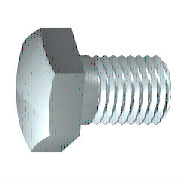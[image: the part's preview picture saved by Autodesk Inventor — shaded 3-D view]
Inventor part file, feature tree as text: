
AUTODESK INVENTOR PART (.ipt)
format: ipt  version: 2025.1 (Build 291241020, 241B)  size: 198,144 bytes
history: native  units: mm (DEFAULTED — no unit token found)
features: extrude x1, chamfer x1, plane x1
ambient origin geometry x7: Origin, YZ Plane, XZ Plane, X Axis, Y Axis, Z Axis, Center Point
bodies: Solid1 (feature_tree), Body (feature_tree)
feature tree (3):
  extrude  "Head"  Depth=40.0mm
  chamfer  "Chamfer1"  Distance=34.0mm
  plane  "Work Plane1"
